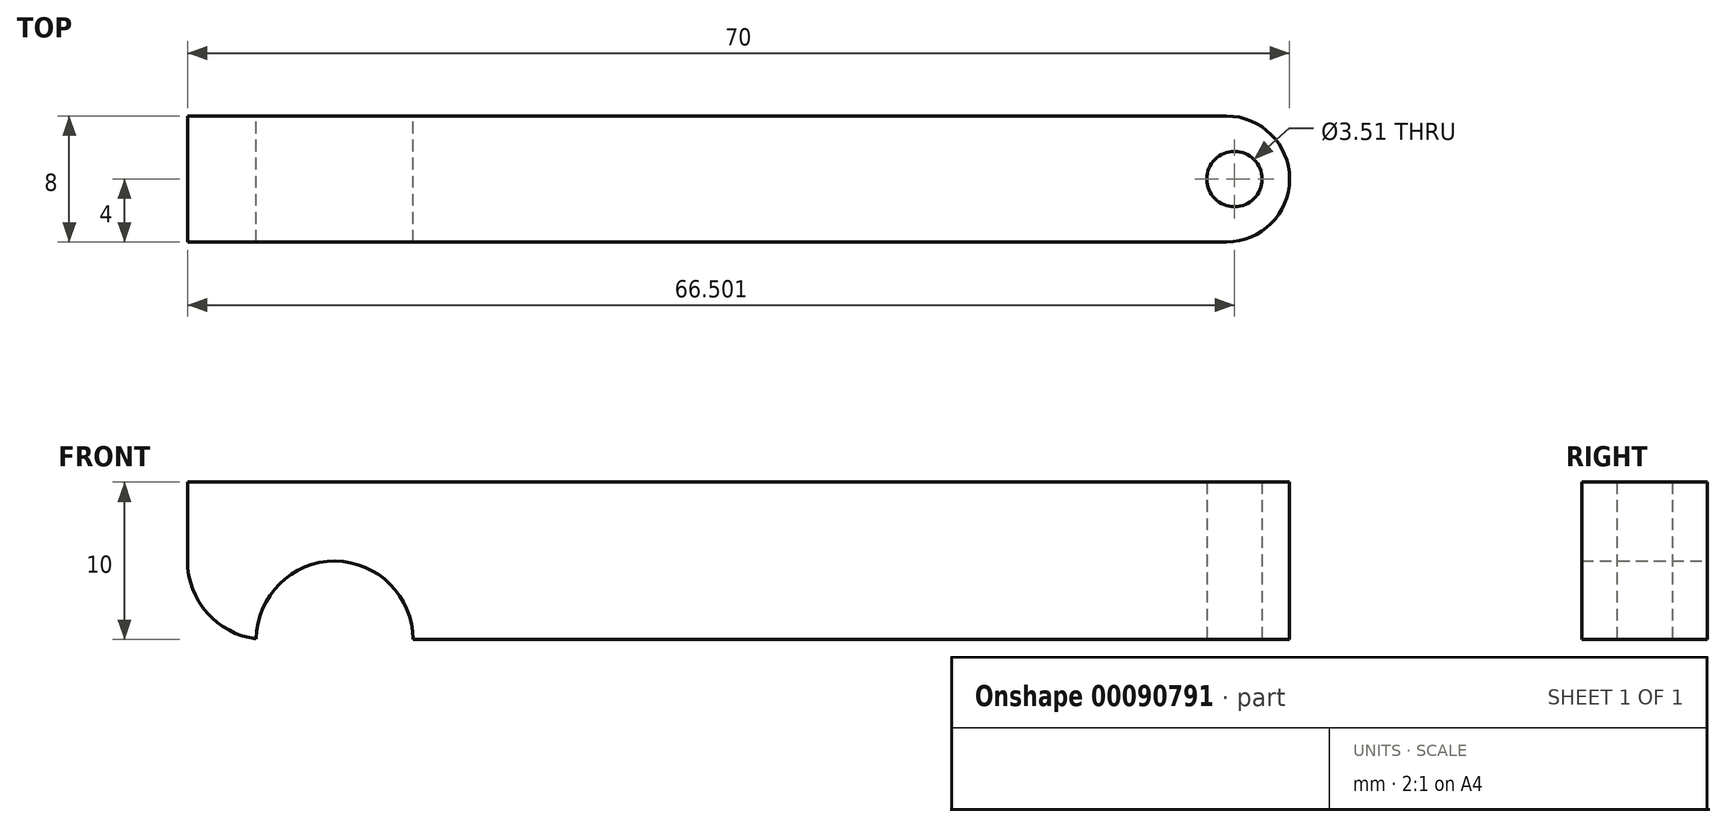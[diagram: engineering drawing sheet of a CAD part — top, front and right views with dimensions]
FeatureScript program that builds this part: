
annotation { "Feature Type Name" : "Feature", "Feature Type Description" : "" }
export const myFeature = defineFeature(function(context is Context, id is Id, definition is map)
    precondition{}
    {
        {
            var Q0;
            Q0=qCreatedBy(makeId("Top.planeOp"),FACE);
            var sketch = newSketch(context, id + "F0", { "sketchPlane" : qUnion([Q0])});
            skLineSegment(sketch, "E0", {"start": v(0, 0) * mm, "end": v(66, 0) * mm});
            skLineSegment(sketch, "E1", {"start": v(70, 4) * mm, "end": v(70, 4) * mm});
            skLineSegment(sketch, "E2", {"start": v(66, 8) * mm, "end": v(0, 8) * mm});
            skLineSegment(sketch, "E3", {"start": v(0, 8) * mm, "end": v(0, 0) * mm});
            skPoint(sketch, "E4.visualSharp", {"position": v(70, 8) * mm});
            skArc(sketch, "E4.filletArc", {"start": v(70, 4) * mm, "mid": v(68.83, 6.83) * mm, "end": v(66, 8) * mm});
            skPoint(sketch, "E5.visualSharp", {"position": v(70, 0) * mm});
            skArc(sketch, "E5.filletArc", {"start": v(66, 0) * mm, "mid": v(68.83, 1.17) * mm, "end": v(70, 4) * mm});
            skSolve(sketch);
        }
        {
            var Q0;
            Q0 = qSketchRegion(id + "F0", true);
            extrude(context, id + "F1", {"entities" : qUnion([Q0]), "depth" : 10 * mm});
        }
        {
            var Q0;
            Q0=makeQuery(id+"F1.opExtrude","CAP_EDGE",EDGE,{"disambiguationData":[OSD([sQuery(id+"F0.wireOp",EDGE,"E3")])],"isStart":true});
            fillet(context, id + "F2", {"entities" : qUnion([Q0]), "radius" : 5 * mm, "tangentPropagation" : true, "allowEdgeOverflow" : false});
        }
        {
            var Q0;
            Q0=makeQuery(id+"F1.opExtrude","SWEPT_FACE",FACE,{"disambiguationData":[OSD([sQuery(id+"F0.wireOp",EDGE,"E2")])]});
            var sketch = newSketch(context, id + "F3", { "sketchPlane" : qUnion([Q0])});
            skCircle(sketch, "E6", {"center": v(-9.35, 0) * mm, "radius": 4.98 * mm});
            skSolve(sketch);
        }
        {
            var Q0;
            Q0 = qSketchRegion(id + "F3", true);
            extrude(context, id + "F4", {"entities" : qUnion([Q0]), "operationType" : NewBodyOperationType.REMOVE, "oppositeDirection" : true, "depth" : 25 * mm});
        }
        {
            var Q0;
            Q0=makeQuery(id+"F1.opExtrude","CAP_FACE",FACE,{"disambiguationData":[OSD([sQuery(id+"F0.wireOp",EDGE,"E0"),sQuery(id+"F0.wireOp",EDGE,"E2"),sQuery(id+"F0.wireOp",EDGE,"E3"),sQuery(id+"F0.wireOp",EDGE,"E4.filletArc"),sQuery(id+"F0.wireOp",EDGE,"E5.filletArc")])],"isStart":true});
            var sketch = newSketch(context, id + "F5", { "sketchPlane" : qUnion([Q0])});
            skCircle(sketch, "E7", {"center": v(66.5, -4) * mm, "radius": 1.76 * mm});
            skPoint(sketch, "E7.centerSnap0", {"position": v(70, -4) * mm});
            skSolve(sketch);
        }
        {
            var Q0;
            Q0 = qSketchRegion(id + "F5", true);
            extrude(context, id + "F6", {"entities" : qUnion([Q0]), "operationType" : NewBodyOperationType.REMOVE, "oppositeDirection" : true, "depth" : 25 * mm});
        }
    });
